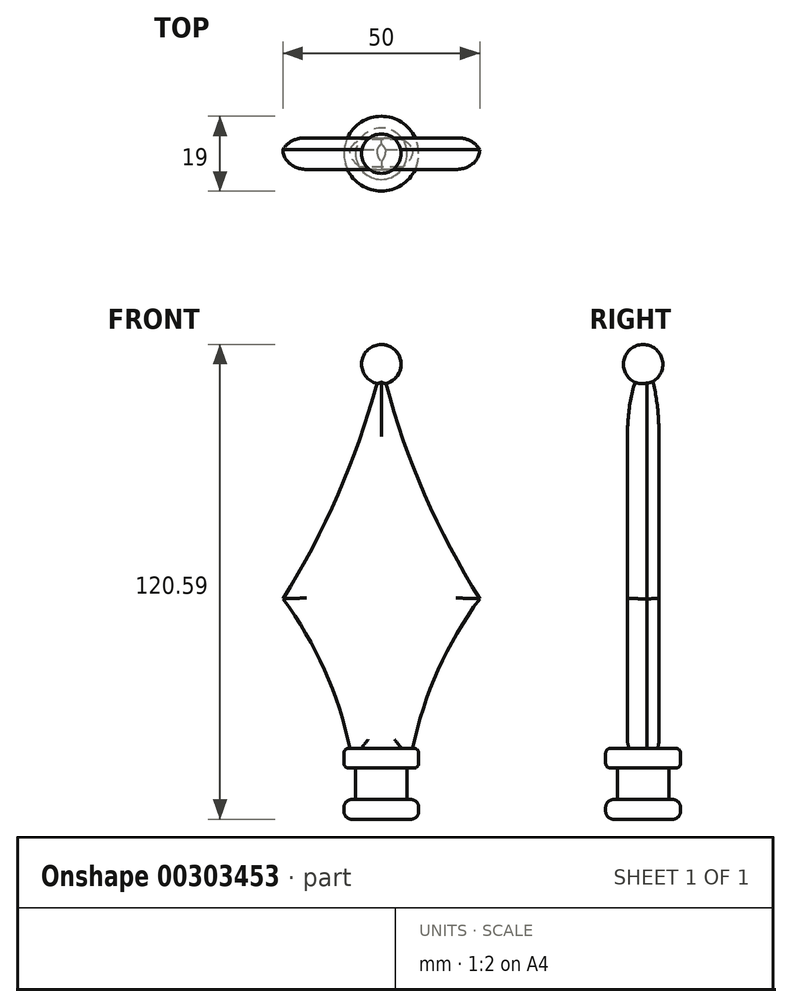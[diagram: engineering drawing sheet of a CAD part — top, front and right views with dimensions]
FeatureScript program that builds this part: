
annotation { "Feature Type Name" : "Feature", "Feature Type Description" : "" }
export const myFeature = defineFeature(function(context is Context, id is Id, definition is map)
    precondition{}
    {
        {
            var Q0;
            Q0=qCreatedBy(makeId("Front.planeOp"),FACE);
            var sketch = newSketch(context, id + "F0", { "sketchPlane" : qUnion([Q0])});
            skLineSegment(sketch, "E0", {"start": v(-7.43, -40.73) * mm, "end": v(0, -40.73) * mm});
            skPoint(sketch, "E1", {"position": v(-12.5, 29.63) * mm});
            skPoint(sketch, "E2", {"position": v(-16.21, -20.37) * mm});
            skLineSegment(sketch, "E3.MirrorCS", {"start": v(7.43, -40.73) * mm, "end": v(0, -40.73) * mm});
            skPoint(sketch, "E4.MirrorP", {"position": v(12.5, 29.63) * mm});
            skArc(sketch, "E5", {"start": v(0, 59.27) * mm, "mid": v(10.1, 28.62) * mm, "end": v(25, 0) * mm});
            skArc(sketch, "E6.MirrorCS", {"start": v(0, 59.27) * mm, "mid": v(-10.1, 28.62) * mm, "end": v(-25, 0) * mm});
            skArc(sketch, "E7", {"start": v(25, 0) * mm, "mid": v(13.87, -19.35) * mm, "end": v(7.43, -40.73) * mm});
            skArc(sketch, "E8.MirrorCS", {"start": v(-25, 0) * mm, "mid": v(-13.87, -19.35) * mm, "end": v(-7.43, -40.73) * mm});
            skSolve(sketch);
        }
        {
            var Q0;
            Q0=makeQuery(id+"F0.imprint","IMPRINT",FACE,{"disambiguationData":[TD([[makeQuery(id+"F0.imprint","IMPRINT",EDGE,{"derivedFrom":sQuery(id+"F0.wireOp",EDGE,"3ipcivuH-bxJN-KwCs-8XCS-91mAZLiwXDlz")}),1.0]])]});
            var Q1;
            Q1=makeQuery(id+"F0.imprint","IMPRINT",FACE,{"disambiguationData":[TD([[makeQuery(id+"F0.imprint","IMPRINT",EDGE,{"derivedFrom":sQuery(id+"F0.wireOp",EDGE,"E0")}),1.0]])]});
            extrude(context, id + "F1", {"entities" : qUnion([Q0, Q1]), "endBound" : BoundingType.SYMMETRIC, "depth" : 8 * mm});
        }
        {
            var Q0;
            Q0=makeQuery(id+"F1.opExtrude","CAP_FACE",FACE,{"disambiguationData":[OSD([sQuery(id+"F0.wireOp",EDGE,"3ipcivuH-bxJN-KwCs-8XCS-91mAZLiwXDlz"),sQuery(id+"F0.wireOp",EDGE,"155COe9Q-MZXf-OWUQ-bgmh-QFCYA2SkLBNz"),sQuery(id+"F0.wireOp",EDGE,"E0"),sQuery(id+"F0.wireOp",EDGE,"E3.MirrorCS"),sQuery(id+"F0.wireOp",EDGE,"d522deef-4d6e-482f-841f-9e26d589a0d61.MirrorCS"),sQuery(id+"F0.wireOp",EDGE,"d522deef-4d6e-482f-841f-9e26d589a0d62.MirrorCS")])],"isStart":false});
            fillet(context, id + "F2", {"entities" : qUnion([Q0]), "radius" : 5 * mm, "tangentPropagation" : true, "allowEdgeOverflow" : false});
        }
        {
            var Q0;
            Q0=makeQuery(id+"F1.opExtrude","CAP_FACE",FACE,{"disambiguationData":[OSD([sQuery(id+"F0.wireOp",EDGE,"3ipcivuH-bxJN-KwCs-8XCS-91mAZLiwXDlz"),sQuery(id+"F0.wireOp",EDGE,"155COe9Q-MZXf-OWUQ-bgmh-QFCYA2SkLBNz"),sQuery(id+"F0.wireOp",EDGE,"E0"),sQuery(id+"F0.wireOp",EDGE,"E3.MirrorCS"),sQuery(id+"F0.wireOp",EDGE,"d522deef-4d6e-482f-841f-9e26d589a0d61.MirrorCS"),sQuery(id+"F0.wireOp",EDGE,"d522deef-4d6e-482f-841f-9e26d589a0d62.MirrorCS")])],"isStart":true});
            fillet(context, id + "F3", {"entities" : qUnion([Q0]), "radius" : 5 * mm, "tangentPropagation" : true, "allowEdgeOverflow" : false});
        }
        {
            var Q0;
            Q0=qCreatedBy(makeId("Front.planeOp"),FACE);
            var sketch = newSketch(context, id + "F4", { "sketchPlane" : qUnion([Q0])});
            skArc(sketch, "E9", {"start": v(0, 64.6) * mm, "mid": v(-5.01, 59.58) * mm, "end": v(0, 54.57) * mm});
            skLineSegment(sketch, "E10", {"start": v(0, 59.58) * mm, "end": v(0, 0) * mm, "construction": true});
            skLineSegment(sketch, "E11", {"start": v(0, 64.6) * mm, "end": v(0, 54.57) * mm});
            skSolve(sketch);
        }
        {
            var Q0;
            Q0=makeQuery(id+"F4.imprint","IMPRINT",FACE,{"disambiguationData":[TD([[makeQuery(id+"F4.imprint","IMPRINT",EDGE,{"derivedFrom":sQuery(id+"F4.wireOp",EDGE,"E9")}),1.0]])]});
            var Q1;
            Q1=sQuery(id+"F4.wireOp",EDGE,"E10");
            revolve(context, id + "F5", {"operationType" : NewBodyOperationType.ADD, "entities" : qUnion([Q0]), "axis" : qUnion([Q1]), "revolveType" : RevolveType.FULL});
        }
        {
            var Q0;
            Q0=qCreatedBy(makeId("Top.planeOp"),FACE);
            cPlane(context, id + "F6", {"entities" : qUnion([Q0]), "cplaneType" : CPlaneType.OFFSET, "offset" : 38 * mm, "oppositeDirection" : true, "width" : 150 * mm, "height" : 150 * mm});
        }
        {
            var Q0;
            Q0=qCreatedBy(id+"F6.planeOp",FACE);
            var sketch = newSketch(context, id + "F7", { "sketchPlane" : qUnion([Q0])});
            skCircle(sketch, "E12", {"center": v(0, 0) * mm, "radius": 9.5 * mm});
            skSolve(sketch);
        }
        {
            var Q0;
            Q0=makeQuery(id+"F7.imprint","IMPRINT",FACE,{"disambiguationData":[TD([[makeQuery(id+"F7.imprint","IMPRINT",EDGE,{"derivedFrom":sQuery(id+"F7.wireOp",EDGE,"E12")}),1.0]])]});
            extrude(context, id + "F8", {"entities" : qUnion([Q0]), "operationType" : NewBodyOperationType.ADD, "oppositeDirection" : true, "depth" : 5 * mm});
        }
        {
            var Q0;
            Q0=makeQuery(id+"F8.opExtrude","CAP_EDGE",EDGE,{"disambiguationData":[OSD([sQuery(id+"F7.wireOp",EDGE,"E12")])],"isStart":false});
            var Q1;
            Q1=makeQuery(id+"F8.opExtrude","CAP_EDGE",EDGE,{"disambiguationData":[OSD([sQuery(id+"F7.wireOp",EDGE,"E12")])],"isStart":true});
            fillet(context, id + "F9", {"entities" : qUnion([Q0, Q1]), "radius" : 1.2 * mm, "allowEdgeOverflow" : false});
        }
        {
            var Q0;
            Q0=makeQuery(id+"F8.opExtrude","CAP_FACE",FACE,{"disambiguationData":[OSD([sQuery(id+"F7.wireOp",EDGE,"E12")])],"isStart":false});
            var sketch = newSketch(context, id + "F10", { "sketchPlane" : qUnion([Q0])});
            skCircle(sketch, "E13", {"center": v(0, 0) * mm, "radius": 6.53 * mm});
            skSolve(sketch);
        }
        {
            var Q0;
            Q0=makeQuery(id+"F10.imprint","IMPRINT",FACE,{"disambiguationData":[TD([[makeQuery(id+"F10.imprint","IMPRINT",EDGE,{"derivedFrom":sQuery(id+"F10.wireOp",EDGE,"E13")}),1.0]])]});
            extrude(context, id + "F11", {"entities" : qUnion([Q0]), "operationType" : NewBodyOperationType.ADD, "depth" : 8 * mm});
        }
        {
            var Q0;
            Q0=makeQuery(id+"F11.opExtrude","CAP_FACE",FACE,{"disambiguationData":[OSD([sQuery(id+"F10.wireOp",EDGE,"E13")])],"isStart":false});
            var sketch = newSketch(context, id + "F12", { "sketchPlane" : qUnion([Q0])});
            skCircle(sketch, "E14", {"center": v(0, 0) * mm, "radius": 9.5 * mm});
            skSolve(sketch);
        }
        {
            var Q0;
            Q0=makeQuery(id+"F12.imprint","IMPRINT",FACE,{"disambiguationData":[TD([[makeQuery(id+"F12.imprint","IMPRINT",EDGE,{"derivedFrom":makeQuery(id+"F11.opExtrude","CAP_EDGE",EDGE,{"disambiguationData":[OSD([sQuery(id+"F10.wireOp",EDGE,"E13")])],"isStart":false})}),1.0]])]});
            var Q1;
            Q1=makeQuery(id+"F12.imprint","IMPRINT",FACE,{"disambiguationData":[TD([[makeQuery(id+"F12.imprint","IMPRINT",EDGE,{"derivedFrom":sQuery(id+"F12.wireOp",EDGE,"E14")}),1.0]])]});
            extrude(context, id + "F13", {"entities" : qUnion([Q0, Q1]), "operationType" : NewBodyOperationType.ADD, "depth" : 5 * mm});
        }
        {
            var Q0;
            Q0=makeQuery(id+"F13.opExtrude","CAP_EDGE",EDGE,{"disambiguationData":[OSD([sQuery(id+"F12.wireOp",EDGE,"E14")])],"isStart":true});
            var Q1;
            Q1=makeQuery(id+"F13.opExtrude","CAP_EDGE",EDGE,{"disambiguationData":[OSD([sQuery(id+"F12.wireOp",EDGE,"E14")])],"isStart":false});
            fillet(context, id + "F14", {"entities" : qUnion([Q0, Q1]), "radius" : 2 * mm, "tangentPropagation" : true, "allowEdgeOverflow" : false});
        }
    });
